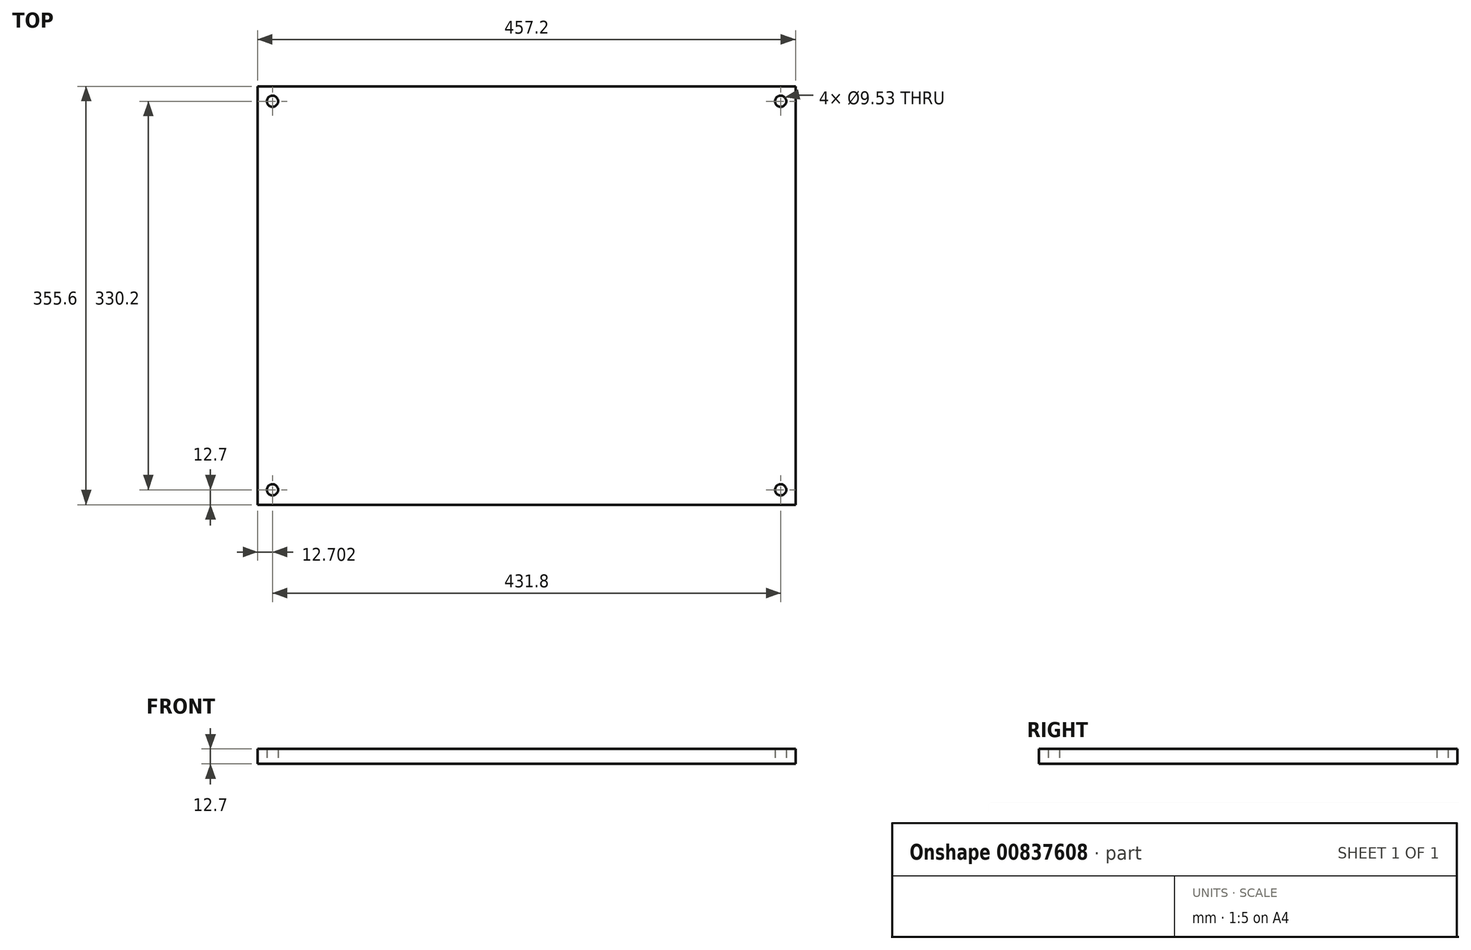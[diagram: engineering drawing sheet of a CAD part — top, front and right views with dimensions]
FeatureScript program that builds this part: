
annotation { "Feature Type Name" : "Feature", "Feature Type Description" : "" }
export const myFeature = defineFeature(function(context is Context, id is Id, definition is map)
    precondition{}
    {
        {
            var Q0;
            Q0=qCreatedBy(makeId("Top.planeOp"),FACE);
            var sketch = newSketch(context, id + "F0", { "sketchPlane" : qUnion([Q0])});
            skLineSegment(sketch, "E0.bottom", {"start": v(97.1, 0) * mm, "end": v(-360.1, 0) * mm});
            skLineSegment(sketch, "E0.top", {"start": v(97.1, 355.6) * mm, "end": v(-360.1, 355.6) * mm});
            skLineSegment(sketch, "E0.left", {"start": v(97.1, 0) * mm, "end": v(97.1, 355.6) * mm});
            skLineSegment(sketch, "E0.right", {"start": v(-360.1, 0) * mm, "end": v(-360.1, 355.6) * mm});
            skCircle(sketch, "E1", {"center": v(-347.4, 342.9) * mm, "radius": 4.76 * mm});
            skCircle(sketch, "E2", {"center": v(84.4, 342.9) * mm, "radius": 4.76 * mm});
            skCircle(sketch, "E3", {"center": v(84.4, 12.7) * mm, "radius": 4.76 * mm});
            skCircle(sketch, "E4", {"center": v(-347.4, 12.7) * mm, "radius": 4.76 * mm});
            skSolve(sketch);
        }
        {
            var Q0;
            Q0=makeQuery(id+"F0.imprint","IMPRINT",FACE,{"disambiguationData":[TD([[makeQuery(id+"F0.imprint","IMPRINT",EDGE,{"derivedFrom":sQuery(id+"F0.wireOp",EDGE,"E0.bottom")}),-1.0]])]});
            extrude(context, id + "F1", {"entities" : qUnion([Q0]), "depth" : 12.7 * mm, "offsetDistance" : 25.4 * mm});
        }
    });
